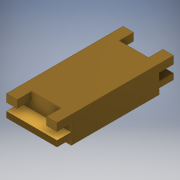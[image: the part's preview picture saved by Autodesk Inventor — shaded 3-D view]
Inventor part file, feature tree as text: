
AUTODESK INVENTOR PART (.ipt)
format: ipt  version: 2019.4 (Build 234330000, 330)  size: 150,528 bytes
history: native  units: in
note: dims shown in document units (in); Inventor stores cm internally (conversion verified against a paired STEP export)
features: extrude x3, sketch x3
ambient origin geometry x8: Origin, YZ Plane, XZ Plane, XY Plane, X Axis, Y Axis, Z Axis, Center Point
bodies: Solid1 (feature_tree)
feature tree (6):
  extrude  "Extrusion1"  Depth=1.0354in
  extrude  "Extrusion2"  Depth=0.2953in
  extrude  "Extrusion3"  Depth=0.1575in TaperAngle=0.0deg
  sketch  "Sketch1"  dims[d0=1.7992in d1=1.0354in]
  sketch  "Sketch2"  dims[d2=0.5512in d3=0.0in d4=0.2953in]
  sketch  "Sketch3"  dims[d5=0.2165in d6=0.1575in d7=0.0in d8=0.1575in d9=0.1181in d10=0.1575in d11=0.1181in d12=1.0354in d13=0.0in]
